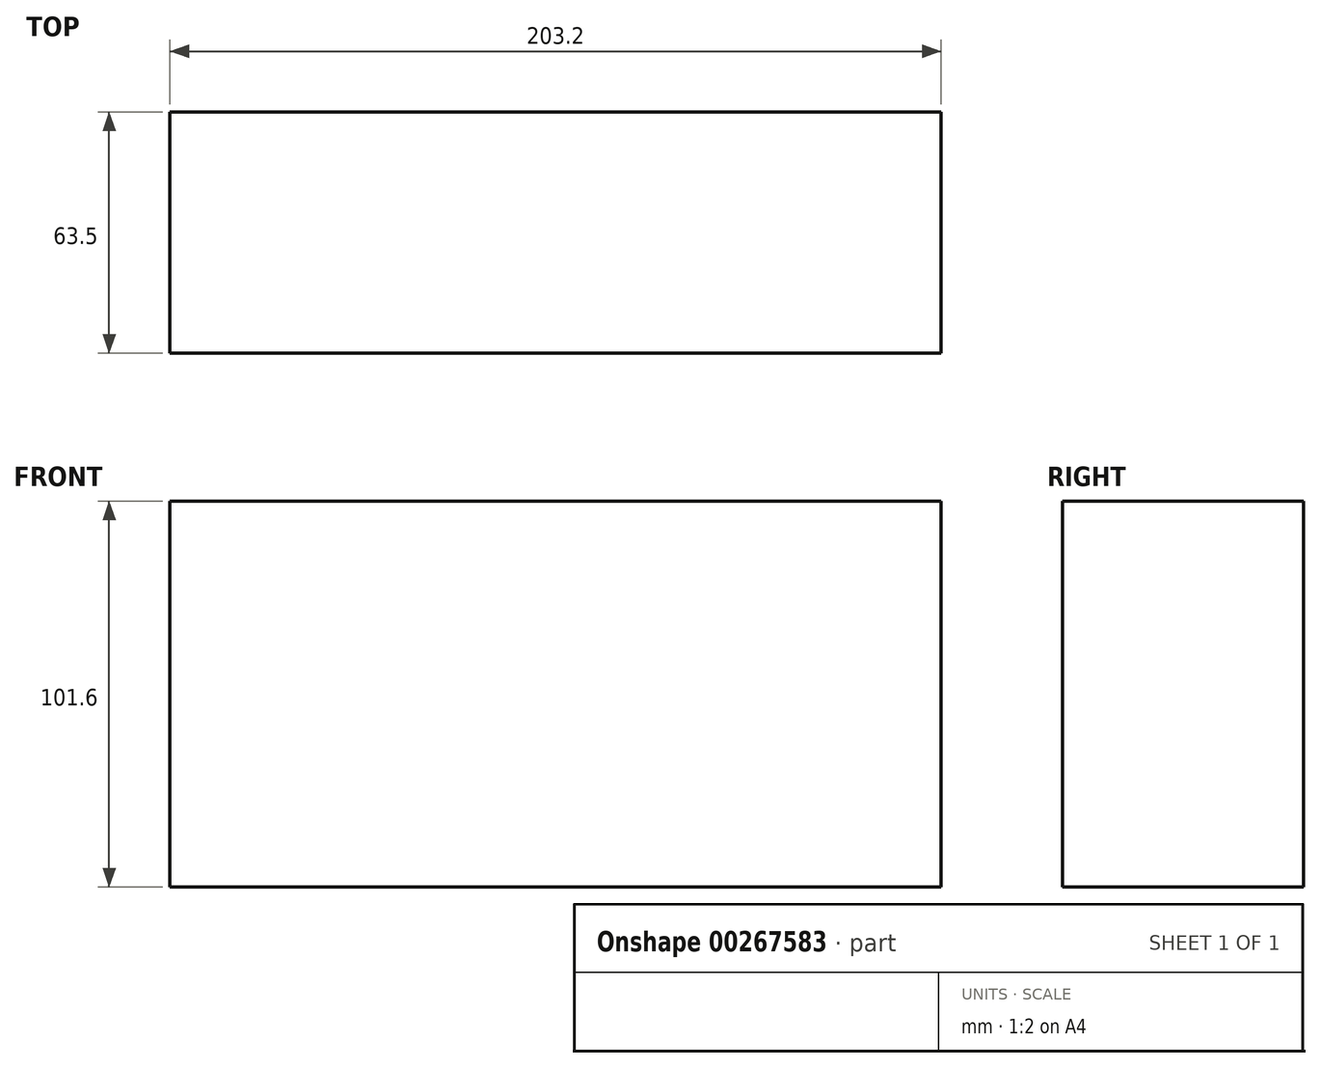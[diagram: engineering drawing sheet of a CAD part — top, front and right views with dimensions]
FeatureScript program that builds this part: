
annotation { "Feature Type Name" : "Feature", "Feature Type Description" : "" }
export const myFeature = defineFeature(function(context is Context, id is Id, definition is map)
    precondition{}
    {
        {
            var Q0;
            Q0=qCreatedBy(makeId("Top.planeOp"),FACE);
            var sketch = newSketch(context, id + "F0", { "sketchPlane" : qUnion([Q0])});
            skLineSegment(sketch, "E0.bottom", {"start": v(0, 0) * mm, "end": v(203.2, 0) * mm});
            skLineSegment(sketch, "E0.top", {"start": v(0, 63.5) * mm, "end": v(203.2, 63.5) * mm});
            skLineSegment(sketch, "E0.left", {"start": v(0, 0) * mm, "end": v(0, 63.5) * mm});
            skLineSegment(sketch, "E0.right", {"start": v(203.2, 0) * mm, "end": v(203.2, 63.5) * mm});
            skSolve(sketch);
        }
        {
            var Q0;
            Q0 = qSketchRegion(id + "F0", true);
            extrude(context, id + "F1", {"entities" : qUnion([Q0]), "depth" : 101.6 * mm});
        }
    });
